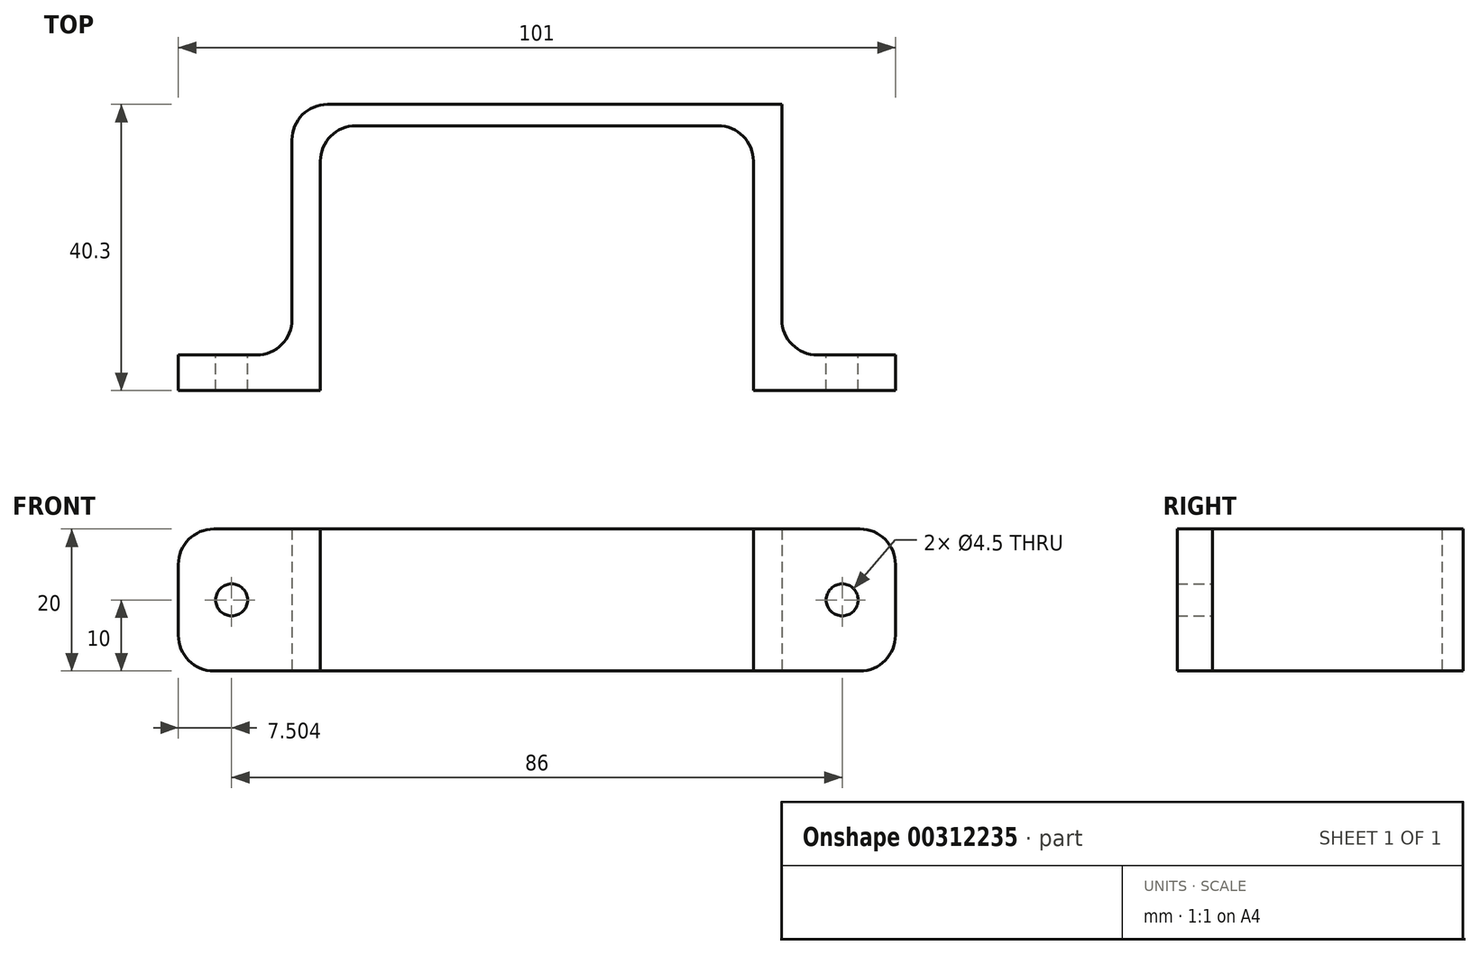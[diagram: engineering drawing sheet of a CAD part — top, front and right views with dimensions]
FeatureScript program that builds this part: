
annotation { "Feature Type Name" : "Feature", "Feature Type Description" : "" }
export const myFeature = defineFeature(function(context is Context, id is Id, definition is map)
    precondition{}
    {
        {
            var Q0;
            Q0=qCreatedBy(makeId("Top.planeOp"),FACE);
            var sketch = newSketch(context, id + "F0", { "sketchPlane" : qUnion([Q0])});
            skLineSegment(sketch, "E0.bottom", {"start": v(-44.1, 0) * mm, "end": v(-24.1, 0) * mm});
            skLineSegment(sketch, "E0.top", {"start": v(-44.1, -5) * mm, "end": v(-24.1, -5) * mm});
            skLineSegment(sketch, "E0.left", {"start": v(-44.1, 0) * mm, "end": v(-44.1, -5) * mm});
            skLineSegment(sketch, "E0.right", {"start": v(-24.1, 0) * mm, "end": v(-24.1, -5) * mm});
            skLineSegment(sketch, "E1.bottom", {"start": v(-24.1, 35.3) * mm, "end": v(40.9, 35.3) * mm});
            skLineSegment(sketch, "E1.top", {"start": v(-24.1, 32.3) * mm, "end": v(40.9, 32.3) * mm});
            skLineSegment(sketch, "E1.left", {"start": v(-24.1, 35.3) * mm, "end": v(-24.1, 32.3) * mm});
            skLineSegment(sketch, "E1.right", {"start": v(40.9, 35.3) * mm, "end": v(40.9, 32.3) * mm});
            skLineSegment(sketch, "E2.bottom", {"start": v(40.9, 35.3) * mm, "end": v(36.9, 35.3) * mm});
            skLineSegment(sketch, "E2.top", {"start": v(40.9, 0) * mm, "end": v(36.9, 0) * mm});
            skLineSegment(sketch, "E2.left", {"start": v(40.9, 35.3) * mm, "end": v(40.9, 0) * mm});
            skLineSegment(sketch, "E2.right", {"start": v(36.9, 35.3) * mm, "end": v(36.9, 0) * mm});
            skLineSegment(sketch, "E3.bottom", {"start": v(36.9, 0) * mm, "end": v(56.9, 0) * mm});
            skLineSegment(sketch, "E3.top", {"start": v(36.9, -5) * mm, "end": v(56.9, -5) * mm});
            skLineSegment(sketch, "E3.left", {"start": v(36.9, 0) * mm, "end": v(36.9, -5) * mm});
            skLineSegment(sketch, "E3.right", {"start": v(56.9, 0) * mm, "end": v(56.9, -5) * mm});
            skLineSegment(sketch, "E4.bottom", {"start": v(-24.1, 35.3) * mm, "end": v(-28.1, 35.3) * mm});
            skLineSegment(sketch, "E4.top", {"start": v(-24.1, 0) * mm, "end": v(-28.1, 0) * mm});
            skLineSegment(sketch, "E4.left", {"start": v(-24.1, 35.3) * mm, "end": v(-24.1, 0) * mm});
            skLineSegment(sketch, "E4.right", {"start": v(-28.1, 35.3) * mm, "end": v(-28.1, 0) * mm});
            skSolve(sketch);
        }
        {
            var Q0;
            Q0 = qSketchRegion(id + "F0", true);
            extrude(context, id + "F1", {"entities" : qUnion([Q0]), "depth" : 20 * mm});
        }
        {
            var Q0;
            Q0=makeQuery(id+"F1.opExtrude","SWEPT_EDGE",EDGE,{"disambiguationData":[OSD([sQuery(id+"F0.wireOp",EDGE,"E1.top"),sQuery(id+"F0.wireOp",EDGE,"E4.left")])]});
            var Q1;
            Q1=makeQuery(id+"F1.opExtrude","SWEPT_EDGE",EDGE,{"disambiguationData":[OSD([sQuery(id+"F0.wireOp",EDGE,"E1.top"),sQuery(id+"F0.wireOp",EDGE,"E2.right")])]});
            fillet(context, id + "F2", {"entities" : qUnion([Q0, Q1]), "radius" : 5 * mm, "tangentPropagation" : true, "allowEdgeOverflow" : false});
        }
        {
            var Q0;
            Q0=makeQuery(id+"F1.opExtrude","SWEPT_FACE",FACE,{"disambiguationData":[OSD([sQuery(id+"F0.wireOp",EDGE,"E0.bottom")])]});
            var sketch = newSketch(context, id + "F3", { "sketchPlane" : qUnion([Q0])});
            skPoint(sketch, "E5", {"position": v(36.6, 10) * mm});
            skPoint(sketch, "E5.positionSnap0", {"position": v(44.1, 10) * mm});
            skSolve(sketch);
        }
        {
            var Q0;
            Q0=makeQuery(id+"F1.opExtrude","SWEPT_FACE",FACE,{"disambiguationData":[OSD([sQuery(id+"F0.wireOp",EDGE,"E3.bottom")])]});
            var sketch = newSketch(context, id + "F4", { "sketchPlane" : qUnion([Q0])});
            skPoint(sketch, "E6", {"position": v(-49.4, 10) * mm});
            skPoint(sketch, "E6.positionSnap0", {"position": v(-56.9, 10) * mm});
            skSolve(sketch);
        }
        {
            var Q0;
            Q0=sQuery(id+"F3.wireOp",VERTEX,"E5");
            var Q1;
            Q1=sQuery(id+"F4.wireOp",VERTEX,"E6");
            var Q2;
            Q2=makeQuery(id+"F1.opExtrude","SWEPT_BODY",BODY,{"disambiguationData":[OSD([sQuery(id+"F0.wireOp",EDGE,"E0.bottom"),sQuery(id+"F0.wireOp",EDGE,"E0.top"),sQuery(id+"F0.wireOp",EDGE,"E0.left"),sQuery(id+"F0.wireOp",EDGE,"E0.right"),sQuery(id+"F0.wireOp",EDGE,"E1.bottom"),sQuery(id+"F0.wireOp",EDGE,"E1.top"),sQuery(id+"F0.wireOp",EDGE,"E2.bottom"),sQuery(id+"F0.wireOp",EDGE,"E2.left"),sQuery(id+"F0.wireOp",EDGE,"E2.right"),sQuery(id+"F0.wireOp",EDGE,"E3.bottom"),sQuery(id+"F0.wireOp",EDGE,"E3.top"),sQuery(id+"F0.wireOp",EDGE,"E3.left"),sQuery(id+"F0.wireOp",EDGE,"E3.right"),sQuery(id+"F0.wireOp",EDGE,"E4.bottom"),sQuery(id+"F0.wireOp",EDGE,"E4.left"),sQuery(id+"F0.wireOp",EDGE,"E4.right")])]});
            hole(context, id + "F5", {"style" : HoleStyle.SIMPLE, "endStyle" : HoleEndStyle.THROUGH, "holeDiameter" : 4.5 * mm, "isTappedThrough" : true, "tappedDepth" : 12 * mm, "tapClearance" : 3, "locations" : qUnion([Q0, Q1]), "scope" : qUnion([Q2])});
        }
        {
            var Q0;
            Q0=makeQuery(id+"F1.opExtrude","SWEPT_EDGE",EDGE,{"disambiguationData":[OSD([sQuery(id+"F0.wireOp",EDGE,"E4.bottom"),sQuery(id+"F0.wireOp",EDGE,"E4.right")])]});
            var Q1;
            Q1=makeQuery(id+"F1.opExtrude","SWEPT_EDGE",EDGE,{"disambiguationData":[OSD([sQuery(id+"F0.wireOp",EDGE,"E2.bottom"),sQuery(id+"F0.wireOp",EDGE,"E2.left")])]});
            fillet(context, id + "F6", {"entities" : qUnion([Q0, Q1]), "radius" : 5 * mm, "tangentPropagation" : true, "allowEdgeOverflow" : false});
        }
        {
            var Q0;
            Q0=makeQuery(id+"F1.opExtrude","SWEPT_EDGE",EDGE,{"disambiguationData":[OSD([sQuery(id+"F0.wireOp",EDGE,"E0.bottom"),sQuery(id+"F0.wireOp",EDGE,"E4.top"),sQuery(id+"F0.wireOp",EDGE,"E4.right")])]});
            var Q1;
            Q1=makeQuery(id+"F1.opExtrude","SWEPT_EDGE",EDGE,{"disambiguationData":[OSD([sQuery(id+"F0.wireOp",EDGE,"E2.left"),sQuery(id+"F0.wireOp",EDGE,"E3.bottom")])]});
            fillet(context, id + "F7", {"entities" : qUnion([Q0, Q1]), "radius" : 5 * mm, "tangentPropagation" : true, "allowEdgeOverflow" : false});
        }
        {
            var Q0;
            Q0=makeQuery(id+"F1.opExtrude","CAP_EDGE",EDGE,{"disambiguationData":[OSD([sQuery(id+"F0.wireOp",EDGE,"E3.right")])],"isStart":false});
            var Q1;
            Q1=makeQuery(id+"F1.opExtrude","CAP_EDGE",EDGE,{"disambiguationData":[OSD([sQuery(id+"F0.wireOp",EDGE,"E3.right")])],"isStart":true});
            var Q2;
            Q2=makeQuery(id+"F1.opExtrude","CAP_EDGE",EDGE,{"disambiguationData":[OSD([sQuery(id+"F0.wireOp",EDGE,"E0.left")])],"isStart":true});
            var Q3;
            Q3=makeQuery(id+"F1.opExtrude","CAP_EDGE",EDGE,{"disambiguationData":[OSD([sQuery(id+"F0.wireOp",EDGE,"E0.left")])],"isStart":false});
            fillet(context, id + "F8", {"entities" : qUnion([Q0, Q1, Q2, Q3]), "radius" : 5 * mm, "tangentPropagation" : true, "allowEdgeOverflow" : false});
        }
    });
